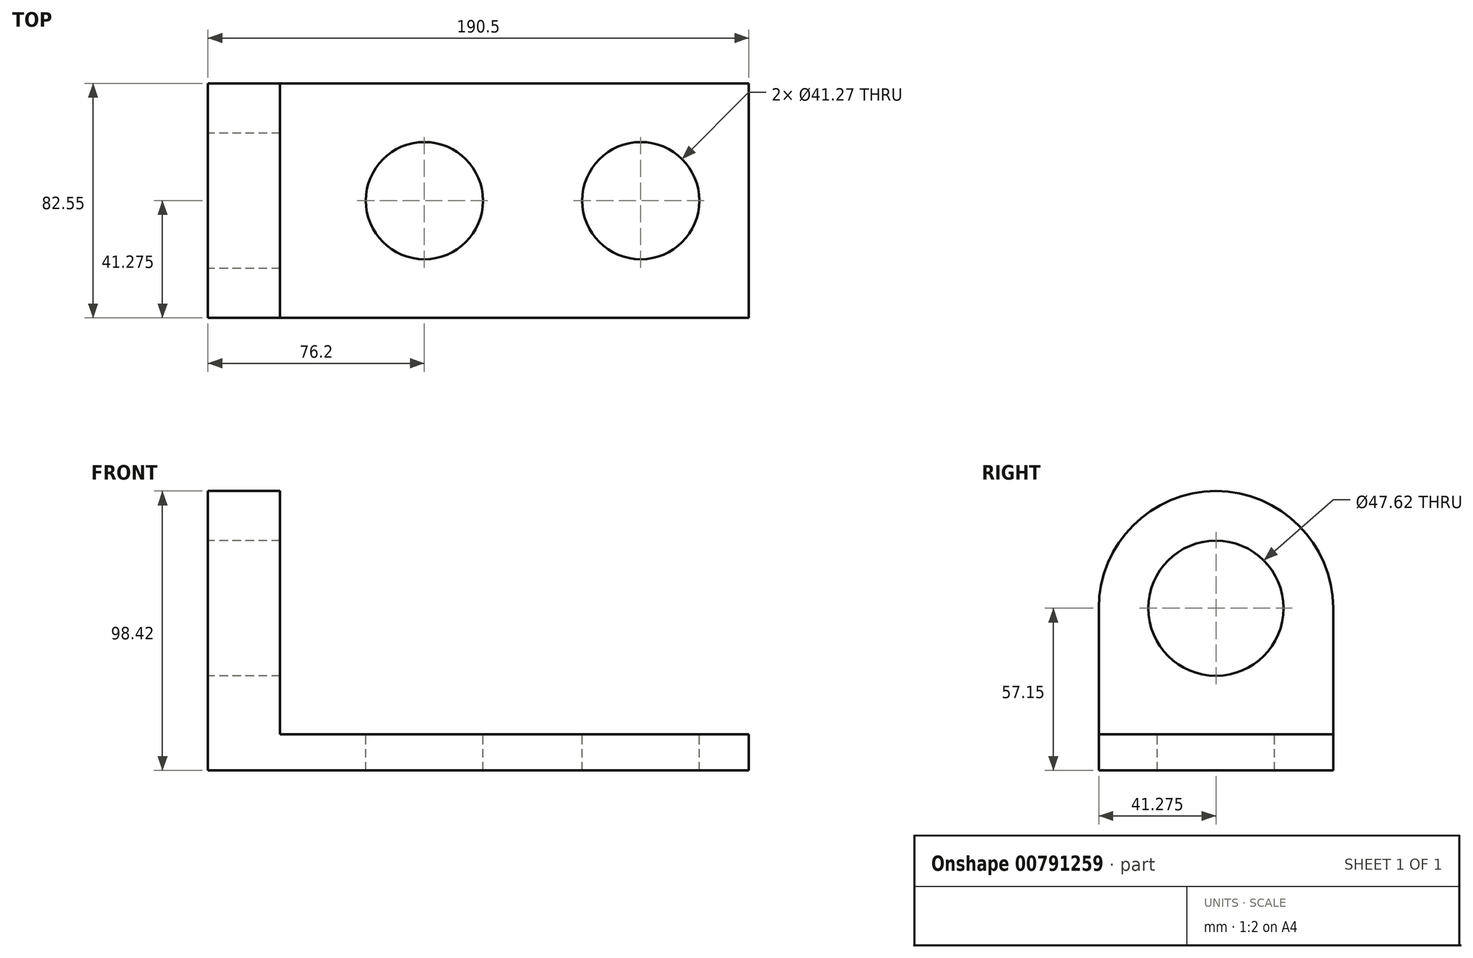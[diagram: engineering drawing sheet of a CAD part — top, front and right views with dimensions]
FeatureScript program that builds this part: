
annotation { "Feature Type Name" : "Feature", "Feature Type Description" : "" }
export const myFeature = defineFeature(function(context is Context, id is Id, definition is map)
    precondition{}
    {
        {
            var Q0;
            Q0=qCreatedBy(makeId("Front.planeOp"),FACE);
            var sketch = newSketch(context, id + "F0", { "sketchPlane" : qUnion([Q0])});
            skLineSegment(sketch, "E0", {"start": v(0, 0) * mm, "end": v(190.5, 0) * mm});
            skLineSegment(sketch, "E1", {"start": v(25.4, 12.7) * mm, "end": v(190.5, 12.7) * mm});
            skLineSegment(sketch, "E2", {"start": v(190.5, 12.7) * mm, "end": v(190.5, 0) * mm});
            skLineSegment(sketch, "E3", {"start": v(0, 0) * mm, "end": v(0, 139.7) * mm});
            skLineSegment(sketch, "E4", {"start": v(0, 139.7) * mm, "end": v(25.4, 139.7) * mm});
            skLineSegment(sketch, "E5", {"start": v(25.4, 139.7) * mm, "end": v(25.4, 12.7) * mm});
            skSolve(sketch);
        }
        {
            var Q0;
            Q0=makeQuery(id+"F0.imprint","IMPRINT",FACE,{"disambiguationData":[TD([[makeQuery(id+"F0.imprint","IMPRINT",EDGE,{"derivedFrom":sQuery(id+"F0.wireOp",EDGE,"E0")}),1.0]])]});
            extrude(context, id + "F1", {"entities" : qUnion([Q0]), "depth" : 82.55 * mm, "offsetDistance" : 25.4 * mm});
        }
        {
            var Q0;
            Q0=makeQuery(id+"F1.opExtrude","SWEPT_FACE",FACE,{"disambiguationData":[OSD([sQuery(id+"F0.wireOp",EDGE,"E1")])]});
            var sketch = newSketch(context, id + "F2", { "sketchPlane" : qUnion([Q0])});
            skLineSegment(sketch, "E6", {"start": v(190.5, -41.28) * mm, "end": v(152.4, -41.28) * mm, "construction": true});
            skLineSegment(sketch, "E7", {"start": v(152.4, -41.28) * mm, "end": v(76.2, -41.28) * mm, "construction": true});
            skCircle(sketch, "E8", {"center": v(76.2, -41.28) * mm, "radius": 20.64 * mm});
            skCircle(sketch, "E9", {"center": v(152.4, -41.28) * mm, "radius": 20.64 * mm});
            skSolve(sketch);
        }
        {
            var Q0;
            Q0=makeQuery(id+"F2.imprint","IMPRINT",FACE,{"disambiguationData":[TD([[makeQuery(id+"F2.imprint","IMPRINT",EDGE,{"derivedFrom":sQuery(id+"F2.wireOp",EDGE,"E8")}),1.0]])]});
            var Q1;
            Q1=makeQuery(id+"F2.imprint","IMPRINT",FACE,{"disambiguationData":[TD([[makeQuery(id+"F2.imprint","IMPRINT",EDGE,{"derivedFrom":sQuery(id+"F2.wireOp",EDGE,"E9")}),1.0]])]});
            extrude(context, id + "F3", {"entities" : qUnion([Q0, Q1]), "operationType" : NewBodyOperationType.REMOVE, "endBound" : BoundingType.UP_TO_NEXT, "oppositeDirection" : true, "depth" : 25.4 * mm, "offsetDistance" : 25.4 * mm});
        }
        {
            var Q0;
            Q0=makeQuery(id+"F1.opExtrude","SWEPT_FACE",FACE,{"disambiguationData":[OSD([sQuery(id+"F0.wireOp",EDGE,"E3")])]});
            var sketch = newSketch(context, id + "F4", { "sketchPlane" : qUnion([Q0])});
            skLineSegment(sketch, "E10", {"start": v(0, 0) * mm, "end": v(0, 57.15) * mm, "construction": true});
            skLineSegment(sketch, "E11", {"start": v(82.55, 0) * mm, "end": v(82.55, 57.15) * mm, "construction": true});
            skArc(sketch, "E12", {"start": v(82.55, 57.15) * mm, "mid": v(41.28, 98.43) * mm, "end": v(0, 57.15) * mm});
            skSolve(sketch);
        }
        {
            var Q0;
            {var subQ0=sQuery(id+"F4.wireOp",EDGE,"E12");Q0=makeQuery(id+"F4.imprint","IMPRINT",FACE,{"disambiguationData":[TD([[makeQuery(id+"F4.imprint","IMPRINT",EDGE,{"derivedFrom":subQ0}),-1.0]])]});}
            extrude(context, id + "F5", {"entities" : qUnion([Q0]), "operationType" : NewBodyOperationType.REMOVE, "oppositeDirection" : true, "depth" : 25.4 * mm, "offsetDistance" : 25.4 * mm});
        }
        {
            var Q0;
            Q0=makeQuery(id+"F1.opExtrude","SWEPT_FACE",FACE,{"disambiguationData":[OSD([sQuery(id+"F0.wireOp",EDGE,"E3")])]});
            var sketch = newSketch(context, id + "F6", { "sketchPlane" : qUnion([Q0])});
            skLineSegment(sketch, "E13", {"start": v(0, 57.15) * mm, "end": v(82.55, 57.15) * mm, "construction": true});
            skLineSegment(sketch, "E14", {"start": v(41.28, 0) * mm, "end": v(41.28, 98.43) * mm, "construction": true});
            skCircle(sketch, "E15", {"center": v(41.28, 57.15) * mm, "radius": 23.81 * mm});
            skSolve(sketch);
        }
        {
            var Q0;
            Q0=makeQuery(id+"F6.imprint","IMPRINT",FACE,{"disambiguationData":[TD([[makeQuery(id+"F6.imprint","IMPRINT",EDGE,{"derivedFrom":sQuery(id+"F6.wireOp",EDGE,"E15")}),1.0]])]});
            extrude(context, id + "F7", {"entities" : qUnion([Q0]), "operationType" : NewBodyOperationType.REMOVE, "endBound" : BoundingType.UP_TO_NEXT, "oppositeDirection" : true, "depth" : 25.4 * mm, "offsetDistance" : 25.4 * mm});
        }
    });
